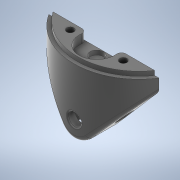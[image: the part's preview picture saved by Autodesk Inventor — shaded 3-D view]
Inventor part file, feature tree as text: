
AUTODESK INVENTOR PART (.ipt)
format: ipt  version: 2020 (Build 240168000, 168)  size: 327,680 bytes
history: native  units: in
note: dims shown in document units (in); Inventor stores cm internally (conversion verified against a paired STEP export)
features: sketch x8, extrude x6, plane x2, hole x2, fillet x2, revolve x1
ambient origin geometry x8: Origin, YZ Plane, XZ Plane, XY Plane, X Axis, Y Axis, Z Axis, Center Point
bodies: Solid1 (feature_tree)
feature tree (21):
  sketch  "Sketch1"  dims[d2=1.75in d3=0.125in]
  revolve  "Revolution1"  [1 undecoded]
  extrude  "Extrusion1"  Depth=0.5in
  extrude  "Extrusion3"  TaperAngle=180.0deg  [1 undecoded]
  extrude  "Extrusion6"  Depth=1.85in TaperAngle=0.0deg
  plane  "Work Plane3"
  hole  "Hole3"  [1 undecoded]
  hole  "Hole4"  [1 undecoded]
  plane  "Work Plane4"
  extrude  "Extrusion9"  Depth=1.2in
  extrude  "Extrusion10"  [1 undecoded]
  extrude  "Extrusion11"  Depth=0.125in
  fillet  "Fillet1"  Radius=0.25in
  fillet  "Fillet2"  Radius=0.25in
  sketch  "Sketch2"  dims[d4=0.1in d5=0.5in]
  sketch  "Sketch8"  dims[d7=0.25in d9=180.0deg]
  sketch  "Sketch9"  dims[d10=1.0in d11=1.85in d12=0.0in]
  sketch  "Sketch10"  dims[d16=1.382in d17=0.0in d38=1.5in]
  sketch  "Sketch14"  dims[d42=1.0in d43=1.2in]
  sketch  "Sketch15"  dims[d44=0.25in d45=0.0in d46=1.2in]
  sketch  "Sketch16"  dims[d47=1.5in d48=0.2031in d49=0.75in d50=0.3125in d51=1.0in d52=0.5635in d53=1.0in d54=0.8108in d55=0.375in d56=0.75in d57=0.5in d58=0.25in d59=0.5635in d60=1.0in d61=0.8108in d67=-0.125in d68=0.5625in d69=0.25in d70=0.0in d71=0.25in d72=0.0in d73=0.375in d74=0.125in d75=0.0in d76=0.0312in d77=0.125in]
note: 5 required parameter values undecoded (feature->parameter linkage not recoverable at this tier; creation-order binding heuristic only, values carry confidence <= 0.55)